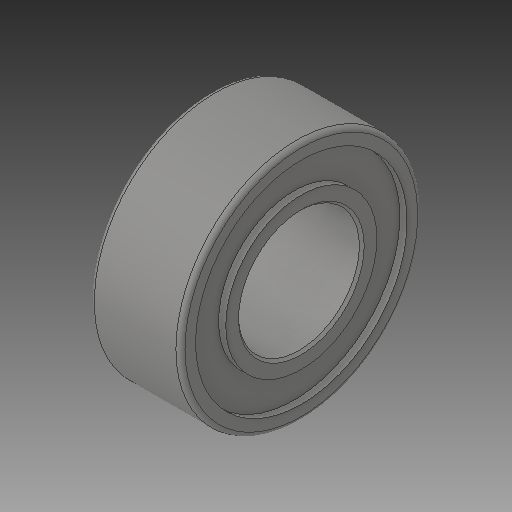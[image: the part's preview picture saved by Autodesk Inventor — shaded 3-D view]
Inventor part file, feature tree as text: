
AUTODESK INVENTOR PART (.ipt)
format: ipt  version: 2017 (Build 210142000, 142)  size: 164,864 bytes
history: native  units: in
note: dims shown in document units (in); Inventor stores cm internally (conversion verified against a paired STEP export)
features: chamfer x1
ambient origin geometry x8: Origin, YZ Plane, XZ Plane, XY Plane, X Axis, Y Axis, Z Axis, Center Point
bodies: Solid1 (feature_tree)
feature tree (1):
  chamfer  "Chamfer1"  [1 undecoded]
note: 1 required parameter value undecoded (feature->parameter linkage not recoverable at this tier; creation-order binding heuristic only, values carry confidence <= 0.55)
